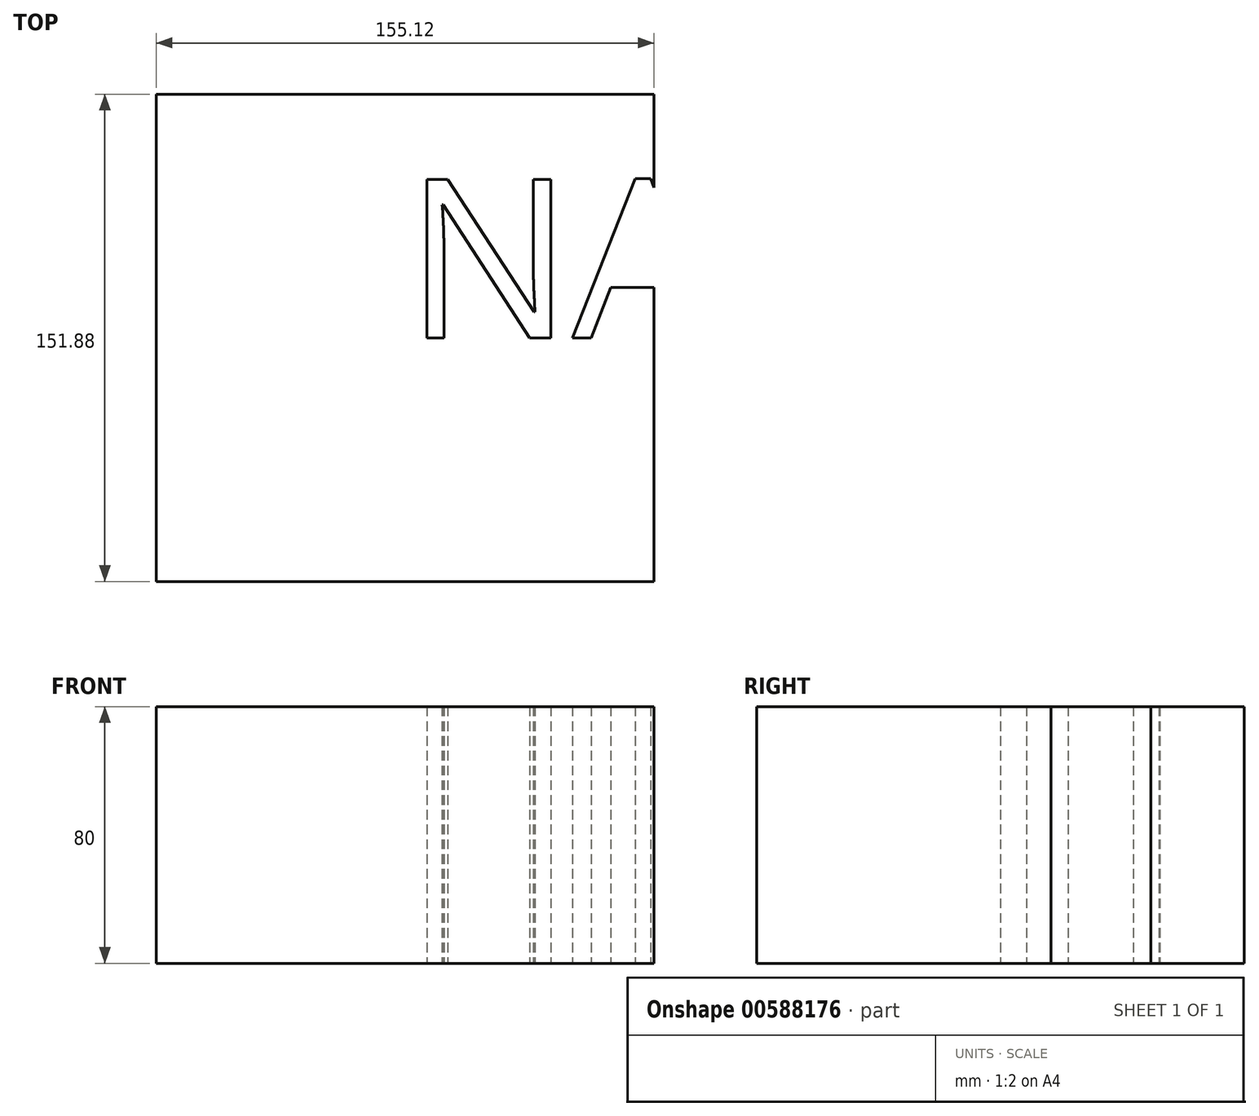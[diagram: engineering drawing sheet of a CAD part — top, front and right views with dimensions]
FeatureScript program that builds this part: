
annotation { "Feature Type Name" : "Feature", "Feature Type Description" : "" }
export const myFeature = defineFeature(function(context is Context, id is Id, definition is map)
    precondition{}
    {
        {
            var Q0;
            Q0=qCreatedBy(makeId("Top.planeOp"),FACE);
            var sketch = newSketch(context, id + "F0", { "sketchPlane" : qUnion([Q0])});
            skPoint(sketch, "E0.middle", {"position": v(0, 0) * mm});
            skLineSegment(sketch, "E1.0", {"start": v(77.56, 75.94) * mm, "end": v(-77.56, 75.94) * mm});
            skLineSegment(sketch, "E1.1", {"start": v(77.56, 75.94) * mm, "end": v(77.56, -75.94) * mm});
            skLineSegment(sketch, "E1.2", {"start": v(77.56, -75.94) * mm, "end": v(-77.56, -75.94) * mm});
            skLineSegment(sketch, "E1.3", {"start": v(-77.56, 75.94) * mm, "end": v(-77.56, -75.94) * mm});
            skText(sketch, "E2", { "text": "NAD", "fontName": "OpenSans-Regular.ttf"});
            const initialGuessF0  = {"E2": [0, 0, 1, 0, 0.0498]};
            skSetInitialGuess(sketch, initialGuessF0);
            skSolve(sketch);
        }
        {
            var Q0;
            Q0=makeQuery(id+"F0.imprint","IMPRINT",FACE,{"disambiguationData":[TD([[makeQuery(id+"F0.imprint","IMPRINT",EDGE,{"derivedFrom":sQuery(id+"F0.wireOp",EDGE,"E1.0")}),1.0]])]});
            extrude(context, id + "F1", {"entities" : qUnion([Q0]), "depth" : 80 * mm, "offsetDistance" : 25 * mm});
        }
    });
